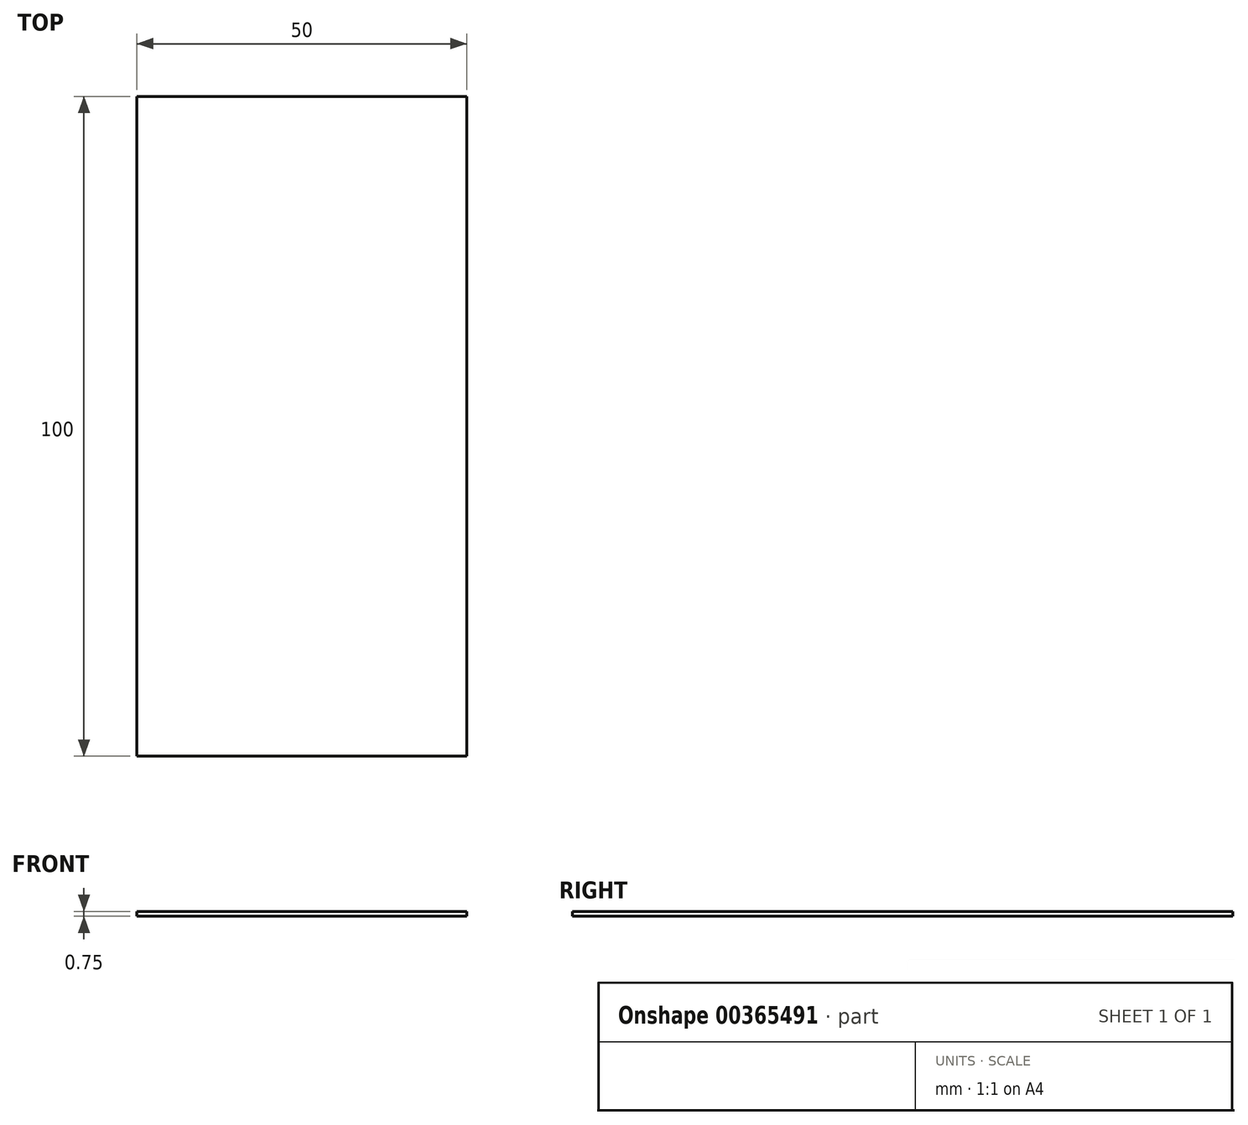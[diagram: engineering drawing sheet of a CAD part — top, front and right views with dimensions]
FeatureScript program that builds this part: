
annotation { "Feature Type Name" : "Feature", "Feature Type Description" : "" }
export const myFeature = defineFeature(function(context is Context, id is Id, definition is map)
    precondition{}
    {
        {
            var Q0;
            Q0=qCreatedBy(makeId("Top.planeOp"),FACE);
            var sketch = newSketch(context, id + "F0", { "sketchPlane" : qUnion([Q0])});
            skLineSegment(sketch, "E0.bottom", {"start": v(25, 50) * mm, "end": v(-25, 50) * mm});
            skLineSegment(sketch, "E0.top", {"start": v(25, -50) * mm, "end": v(-25, -50) * mm});
            skLineSegment(sketch, "E0.left", {"start": v(25, 50) * mm, "end": v(25, -50) * mm});
            skLineSegment(sketch, "E0.right", {"start": v(-25, 50) * mm, "end": v(-25, -50) * mm});
            skPoint(sketch, "E0.middle", {"position": v(0, 0) * mm});
            skSolve(sketch);
        }
        {
            var Q0;
            Q0 = qSketchRegion(id + "F0", true);
            extrude(context, id + "F1", {"entities" : qUnion([Q0]), "depth" : .75 * mm});
        }
    });
